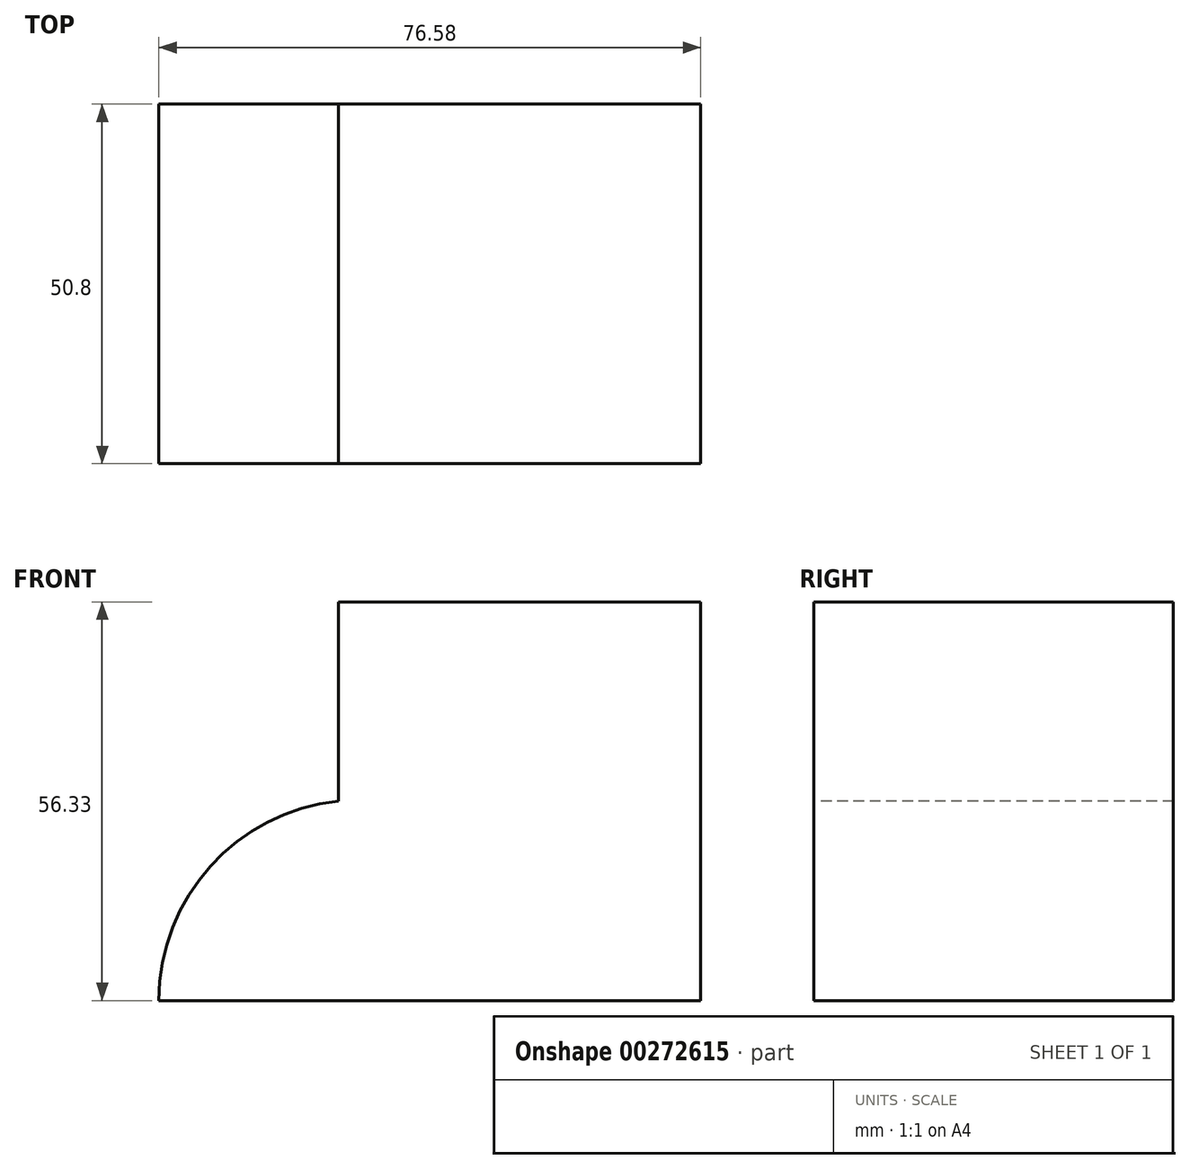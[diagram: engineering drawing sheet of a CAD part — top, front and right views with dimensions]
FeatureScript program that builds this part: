
annotation { "Feature Type Name" : "Feature", "Feature Type Description" : "" }
export const myFeature = defineFeature(function(context is Context, id is Id, definition is map)
    precondition{}
    {
        {
            var Q0;
            Q0=qCreatedBy(makeId("Front.planeOp"),FACE);
            var sketch = newSketch(context, id + "F0", { "sketchPlane" : qUnion([Q0])});
            skLineSegment(sketch, "E0.bottom", {"start": v(-27.3, 56.33) * mm, "end": v(23.87, 56.33) * mm});
            skLineSegment(sketch, "E0.top", {"start": v(-27.3, 0) * mm, "end": v(23.87, 0) * mm});
            skLineSegment(sketch, "E0.left", {"start": v(-27.3, 56.33) * mm, "end": v(-27.3, 0) * mm});
            skLineSegment(sketch, "E0.right", {"start": v(23.87, 56.33) * mm, "end": v(23.87, 0) * mm});
            skSolve(sketch);
        }
        {
            var Q0;
            Q0 = qSketchRegion(id + "F0", true);
            extrude(context, id + "F1", {"entities" : qUnion([Q0]), "depth" : 50.8 * mm});
        }
        {
            var Q0;
            Q0=makeQuery(id+"F1.opExtrude","SWEPT_FACE",FACE,{"disambiguationData":[OSD([sQuery(id+"F0.wireOp",EDGE,"E0.left")])]});
            var sketch = newSketch(context, id + "F2", { "sketchPlane" : qUnion([Q0])});
            skLineSegment(sketch, "E1.bottom", {"start": v(0, 28.17) * mm, "end": v(50.8, 28.17) * mm});
            skLineSegment(sketch, "E1.top", {"start": v(0, 0) * mm, "end": v(50.8, 0) * mm});
            skLineSegment(sketch, "E1.left", {"start": v(0, 28.17) * mm, "end": v(0, 0) * mm});
            skLineSegment(sketch, "E1.right", {"start": v(50.8, 28.17) * mm, "end": v(50.8, 0) * mm});
            skSolve(sketch);
        }
        {
            var Q0;
            Q0 = qSketchRegion(id + "F2", true);
            extrude(context, id + "F3", {"entities" : qUnion([Q0]), "operationType" : NewBodyOperationType.ADD, "depth" : 25.4 * mm});
        }
        {
            var Q0;
            Q0=makeQuery(id+"F3.boolean.opBoolean","MERGE",FACE,{"derivedFrom":[makeQuery(id+"F1.opExtrude","CAP_FACE",FACE,{"disambiguationData":[OSD([sQuery(id+"F0.wireOp",EDGE,"E0.bottom"),sQuery(id+"F0.wireOp",EDGE,"E0.top"),sQuery(id+"F0.wireOp",EDGE,"E0.left"),sQuery(id+"F0.wireOp",EDGE,"E0.right")])],"isStart":false}),makeQuery(id+"F3.opExtrude","SWEPT_FACE",FACE,{"disambiguationData":[OSD([sQuery(id+"F2.wireOp",EDGE,"E1.right")])]})]});
            var sketch = newSketch(context, id + "F4", { "sketchPlane" : qUnion([Q0])});
            skArc(sketch, "E2", {"start": v(-27.3, 28.17) * mm, "mid": v(-45.42, 18.96) * mm, "end": v(-52.7, 0) * mm});
            skLineSegment(sketch, "E3", {"start": v(-52.7, 0) * mm, "end": v(-52.7, 28.17) * mm});
            skSolve(sketch);
        }
        {
            var Q0;
            Q0=makeQuery(id+"F4.imprint","IMPRINT",FACE,{"disambiguationData":[TD([[makeQuery(id+"F4.imprint","IMPRINT",EDGE,{"derivedFrom":sQuery(id+"F4.wireOp",EDGE,"E2")}),-1.0]])]});
            extrude(context, id + "F5", {"entities" : qUnion([Q0]), "operationType" : NewBodyOperationType.REMOVE, "oppositeDirection" : true, "depth" : 50.8 * mm});
        }
    });
